# Revit family: RVi-IPC33VB (2,8 мм)
name_source: partatom
category: Устройства связи
revit_build: Autodesk Revit 2016 (Build: 20161004_0715(x64)
units: mm (PartAtom-declared; Revit-internal decimal feet)

## family parameters
Всегда вертикально = Да
На основе рабочей плоскости = Да
Общий = Нет
При загрузке вырезать с полостями = Нет
Размер круглого соединителя = Использовать диаметр
Сохранять ориентацию аннотаций = Нет
Тип детали = Нормальный
Точка расчета площади = Нет

## types (2) — shared parameters
2D.Телекамера в герметичном термокожухе = Нет
2D.Телекамера с поворотным устройством = Нет
Bullet.корпус = Без корпуса : Пусто
Bullet.крепление = Без крепления : Пусто
Kr_max = 360.00°
Kr_min = -360.00°
RVi.Аудио.Вход = Нет
RVi.Аудио.Выход = Нет
RVi.Аудио.Динамик = Нет
RVi.Аудио.Микрофон = Нет
RVi.ИК подсветка.Дальность = 30000 мм
RVi.Карта памяти = Нет
RVi.Питание 12В = Да
RVi.Питание 24В = Нет
RVi.Питание POE = Да
RVi.Разрешение = 2048×1536
RVi.Тип корпуса = Купольные антивандальные
RVi.Тип продукта = Камеры внутренней установки
RVi.Тревога = Нет
RVi.Функция аналитики = Нет
Rn_max = 90.00°
Rn_min = 0.00°
Ro_max = 360.00°
Ro_min = -360.00°
URL = http://rvi-cctv.ru
Ug_max = 83.00°
Ug_min = 82.50°
Uv_max = 53.00°
Uv_min = 52.50°
Вращение всей камеры = 0.00°
Группа модели = Камера в сборе
Длина неподвижной части корпуса = 51 мм
Изготовитель = RVi
К идентификации = 250
К обнаружения = 20
К распознавания номера = 240
К распознования = 100
Купол.корпус = Корпус 31VB_корпус : Тип
Купол.обектив = Корпус 31VB_объектив : Тип
Купольная камера = Да
Материал корпуса камеры = Камера.корпус
Материал крепления = Камера.крепление
Материал объектива камеры = Камера.объектив
Наименование и техническая характеристика = Антивандальная IP-камера; 1/3” КМОП-матрица, Формат сжатия: H.264/ H.264H/ H.264B/ MJPEG; Максимальное разрешение и скорость трансляции: 2048×1536 (20 к/с); Нижний порог чувствительности: 0.1 лк / F2.0 (Цвет), 0 лк / F2.0 (ИК вкл.);  Мегапиксельный объектив: 2.8 мм; ИК-подсветка: до 30 метров; ONVIF; Класс защиты: IP67, IK10; Диапазон рабочих температур: -40…+60°С; Питание: PoE (802.3af) / DC 12 В, не более 3.5 Вт.
Обектив коррекция наклона = 0.00°
Отметка по умолчанию = 1219 мм
Поворот направления взгляда = 0.00°
Смещение объектива = 35 мм
Стрела угол подъема = 0.00°
УГО смещение = 200 мм
да = Да
нет = Нет
zero-valued in all types: Длина подвижной части

## per-type parameters (varying)
| type | Крепление | Стрела длина | Стрела коррекция |
| Крепление BW4 | Крепление BW4 : Тип | 83 мм | -90.00° |
| Стандартная | Без крепления : Пусто | 0 мм | 0.00° |

## geometry (parser evidence)
native form markers: Blend x14
no freeform markers — native parametric forms only
